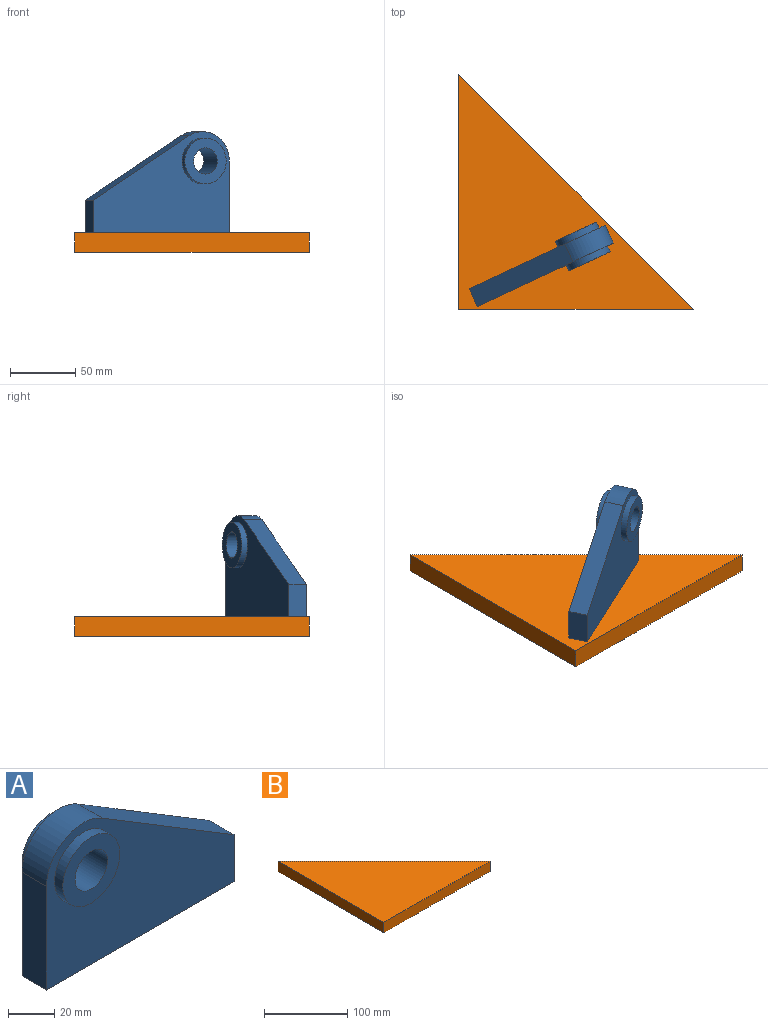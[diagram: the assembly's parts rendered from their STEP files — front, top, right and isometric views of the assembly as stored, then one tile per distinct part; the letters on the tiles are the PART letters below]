
ASSEMBLY  parts=2 mates=1
PART A: 12 faces, bbox 115x25x77.5 mm
  f0: plane 80.8x49.22mm, normal (0.52,0,0.85), area 1419.1mm2, adj f1,f4,f5,f6
  f1: cylinder r=22.5mm len=34.21mm, axis (0,-1,0), area 714.8mm2, adj f0,f2,f5,f6
  f2: plane 55x15mm, normal (-1,0,0), area 825mm2, adj f1,f3,f5,f6
  f3: plane 115x15mm, normal (0,0,-1), area 1725mm2, adj f2,f4,f5,f6
  f4: plane 25x15mm, normal (1,0,0), area 375mm2, adj f0,f3,f5,f6
  f5: plane 115x77.5mm, normal (0,1,0), area 5575.8mm2, adj f0,f1,f2,f3,f4,f10
  f6: plane 115x77.5mm, normal (0,-1,0), area 5575.8mm2, adj f0,f1,f2,f3,f4,f8
  f7: plane 35x35mm, normal (0,-1,0), area 648mm2, adj f8,f9
  f8: cylinder r=17.5mm len=35mm, axis (0,1,0), area 549.8mm2, adj f6,f7
  f9: cylinder r=10mm len=25mm, axis (0,-1,0), area 1570.8mm2, adj f7,f11
  f10: cylinder r=17.5mm len=35mm, axis (0,1,0), area 549.8mm2, adj f5,f11
  f11: plane 35x35mm, normal (0,1,0), area 648mm2, adj f9,f10
PART B: 5 faces, bbox 180x180x15 mm
  f0: plane 180x15mm, normal (-1,0,0), area 2700mm2, adj f1,f2,f3,f4
  f1: plane 180x15mm, normal (0,-1,0), area 2700mm2, adj f0,f2,f3,f4
  f2: plane 180x180mm, normal (0.71,0.71,0), area 3818.4mm2, adj f0,f1,f3,f4
  f3: plane 180x180mm, normal (0,0,1), area 16200mm2, adj f0,f1,f2
  f4: plane 180x180mm, normal (0,0,-1), area 16200mm2, adj f0,f1,f2
PLACE A rot(axis=(0,0,-1),155deg) t=(102.03,33.32,78.47)mm
PLACE B t=(10.12,-21.55,8.47)mm
MATE planar A.f3 <-> B.f3  axis (0,0,-1) through (73.48,11.73,23.47)mm
